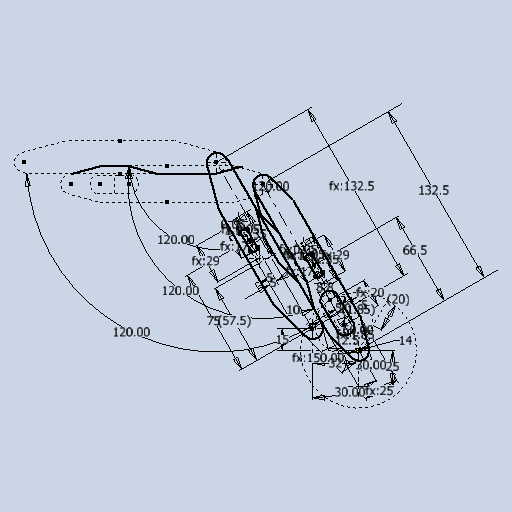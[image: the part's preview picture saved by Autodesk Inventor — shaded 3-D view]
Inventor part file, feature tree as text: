
AUTODESK INVENTOR PART (.ipt)
format: ipt  version: 2024.2 (Build 282272000, 272)  size: 346,112 bytes
history: native  units: mm
features: sketch x1
ambient origin geometry x8: Origin, YZ Plane, XZ Plane, XY Plane, X Axis, Y Axis, Z Axis, Center Point
feature tree (1):
  sketch  "Sketch1"  dims[d0=32.0mm d1=15.0mm d2=25.0mm d3=30.0deg d4=132.5mm d5=25.0mm d6=30.0deg d7=14.0mm d8=132.5mm d11=20.0mm d12=60.0deg d13=20.0mm d14=20.0mm d15=5.0mm d16=8.8mm d17=1.85mm d18=1.85mm d19=5.0mm d20=35.0mm d21=17.0mm d22=1.5mm d23=0.05mm d24=0.05mm d25=29.0mm d26=5.0mm d27=35.0mm d28=17.0mm d29=1.5mm d30=0.05mm d31=0.05mm d32=29.0mm d33=30.0deg d34=5.0mm d36=75.0mm d37=20.0mm d39=120.0deg d41=20.0mm d43=120.0deg d45=20.0mm d47=120.0deg d49=20.0mm d51=120.0deg d53=66.5mm d54=12.5mm d55=10.0mm d56=57.5mm]
